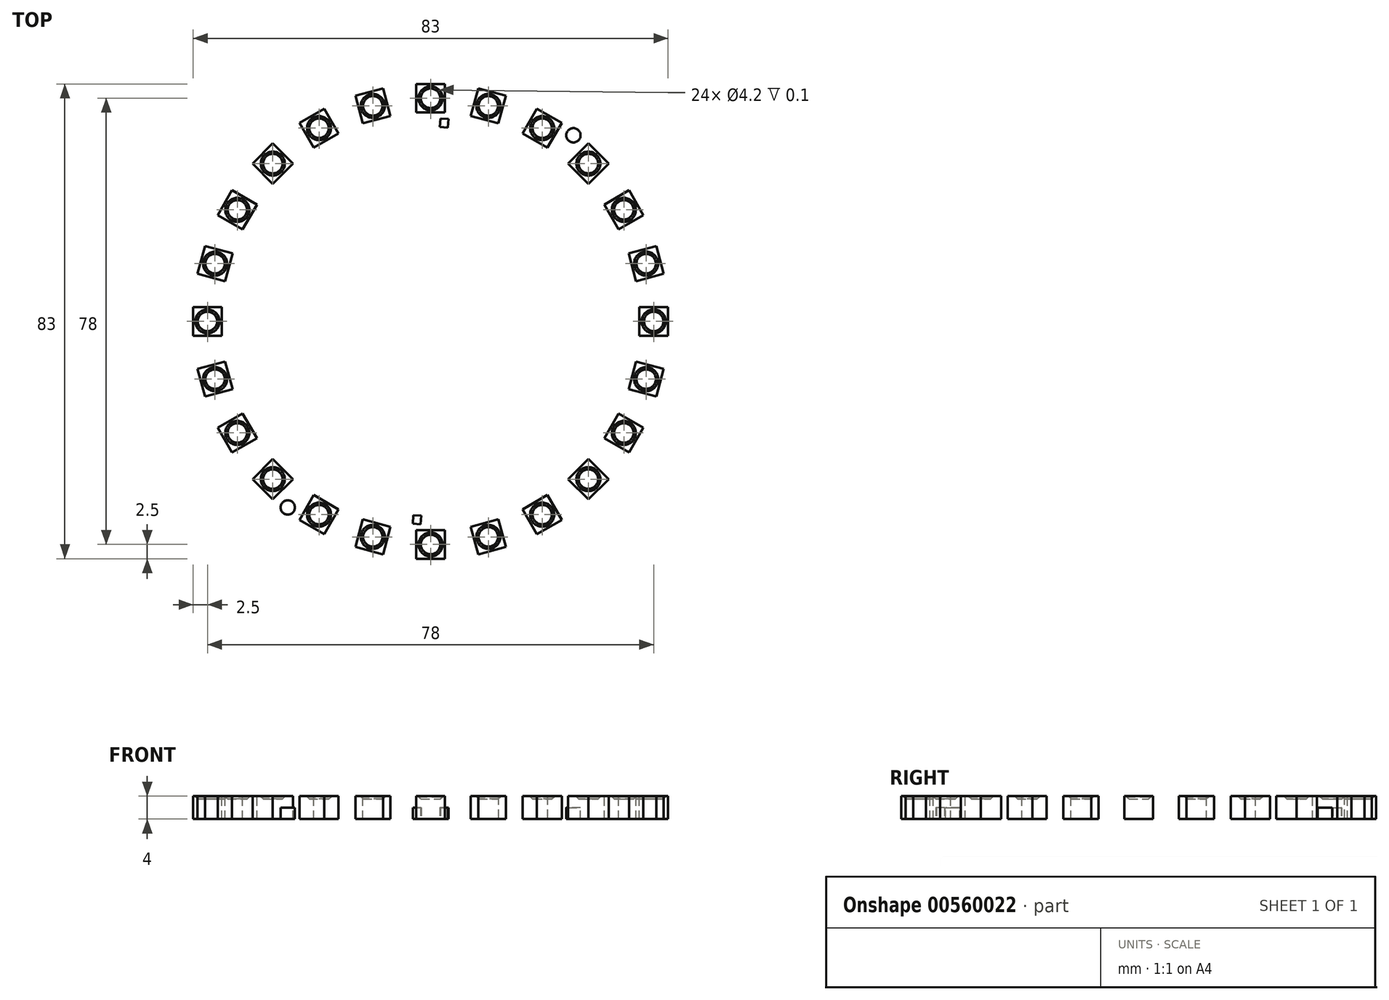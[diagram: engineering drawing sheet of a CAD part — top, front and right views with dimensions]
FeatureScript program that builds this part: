
annotation { "Feature Type Name" : "Feature", "Feature Type Description" : "" }
export const myFeature = defineFeature(function(context is Context, id is Id, definition is map)
    precondition{}
    {
        {
            var Q0;
            Q0=qCreatedBy(makeId("Top.planeOp"),FACE);
            var sketch = newSketch(context, id + "F0", { "sketchPlane" : qUnion([Q0])});
            skCircle(sketch, "E0", {"center": v(0, 0) * mm, "radius": 35.5 * mm});
            skCircle(sketch, "E1", {"center": v(0, 0) * mm, "radius": 42.5 * mm});
            skSolve(sketch);
        }
        {
            var Q0;
            Q0=makeQuery(id+"F0.imprint","IMPRINT",FACE,{"disambiguationData":[TD([[makeQuery(id+"F0.imprint","IMPRINT",EDGE,{"derivedFrom":sQuery(id+"F0.wireOp",EDGE,"E0")}),-1.0]])]});
            extrude(context, id + "F1", {"entities" : qUnion([Q0]), "depth" : 2 * mm, "offsetDistance" : 25 * mm});
        }
        {
            var Q0;
            Q0=makeQuery(id+"F1.opExtrude","CAP_FACE",FACE,{"disambiguationData":[OSD([sQuery(id+"F0.wireOp",EDGE,"E0"),sQuery(id+"F0.wireOp",EDGE,"E1")])],"isStart":false});
            var sketch = newSketch(context, id + "F2", { "sketchPlane" : qUnion([Q0])});
            skLineSegment(sketch, "E2.bottom", {"start": v(2.5, 36.5) * mm, "end": v(-2.5, 36.5) * mm});
            skLineSegment(sketch, "E2.top", {"start": v(2.5, 41.5) * mm, "end": v(-2.5, 41.5) * mm});
            skLineSegment(sketch, "E2.left", {"start": v(2.5, 36.5) * mm, "end": v(2.5, 41.5) * mm});
            skLineSegment(sketch, "E2.right", {"start": v(-2.5, 36.5) * mm, "end": v(-2.5, 41.5) * mm});
            skPoint(sketch, "E2.middle", {"position": v(0, 39) * mm});
            skSolve(sketch);
        }
        {
            var Q0;
            Q0 = qSketchRegion(id + "F2", true);
            extrude(context, id + "F3", {"entities" : qUnion([Q0]), "depth" : 2 * mm, "offsetDistance" : 25 * mm});
        }
        {
            var Q0;
            Q0=makeQuery(id+"F3.opExtrude","CAP_FACE",FACE,{"disambiguationData":[OSD([sQuery(id+"F2.wireOp",EDGE,"E2.bottom"),sQuery(id+"F2.wireOp",EDGE,"E2.top"),sQuery(id+"F2.wireOp",EDGE,"E2.left"),sQuery(id+"F2.wireOp",EDGE,"E2.right")])],"isStart":false});
            var sketch = newSketch(context, id + "F4", { "sketchPlane" : qUnion([Q0])});
            skCircle(sketch, "E3", {"center": v(0, 39) * mm, "radius": 2.1 * mm});
            skPoint(sketch, "E3.centerSnap0", {"position": v(2.5, 39) * mm});
            skPoint(sketch, "E3.centerSnap1", {"position": v(0, 41.5) * mm});
            skSolve(sketch);
        }
        {
            var Q0;
            Q0=makeQuery(id+"F4.imprint","IMPRINT",FACE,{"disambiguationData":[TD([[makeQuery(id+"F4.imprint","IMPRINT",EDGE,{"derivedFrom":sQuery(id+"F4.wireOp",EDGE,"E3")}),1.0]])]});
            extrude(context, id + "F5", {"entities" : qUnion([Q0]), "operationType" : NewBodyOperationType.REMOVE, "oppositeDirection" : true, "depth" : 0.5 * mm, "offsetDistance" : 25 * mm});
        }
        {
            var Q0;
            Q0=makeQuery(id+"F5.boolean.opBoolean","COPY",EDGE,{"derivedFrom":makeQuery(id+"F5.opExtrude","CAP_EDGE",EDGE,{"disambiguationData":[OSD([sQuery(id+"F4.wireOp",EDGE,"E3")])],"isStart":false})});
            chamfer(context, id + "F6", {"entities" : qUnion([Q0]), "width" : 0.4 * mm, "tangentPropagation" : true});
        }
        {
            var Q0;
            Q0=makeQuery(id+"F3.opExtrude","SWEPT_BODY",BODY,{"disambiguationData":[OSD([sQuery(id+"F2.wireOp",EDGE,"E2.bottom"),sQuery(id+"F2.wireOp",EDGE,"E2.top"),sQuery(id+"F2.wireOp",EDGE,"E2.left"),sQuery(id+"F2.wireOp",EDGE,"E2.right")])]});
            var Q1;
            Q1=makeQuery(id+"F1.opExtrude","CAP_EDGE",EDGE,{"disambiguationData":[OSD([sQuery(id+"F0.wireOp",EDGE,"E0")])],"isStart":false});
            circularPattern(context, id + "F7", {"operationType" : NewBodyOperationType.ADD, "entities" : qUnion([Q0]), "axis" : qUnion([Q1]), "angle" : 360 * degree, "instanceCount" : 24, "equalSpace" : true});
        }
        {
            var Q0;
            Q0=makeQuery(id+"F1.opExtrude","CAP_FACE",FACE,{"disambiguationData":[OSD([sQuery(id+"F0.wireOp",EDGE,"E0"),sQuery(id+"F0.wireOp",EDGE,"E1")])],"isStart":false});
            var sketch = newSketch(context, id + "F8", { "sketchPlane" : qUnion([Q0])});
            skLineSegment(sketch, "E4", {"start": v(0, 61.56) * mm, "end": v(0, -60.15) * mm, "construction": true});
            skLineSegment(sketch, "E5", {"start": v(64.53, 0) * mm, "end": v(-72.37, 0) * mm, "construction": true});
            skCircle(sketch, "E6.0", {"center": v(0, 0) * mm, "radius": 42.5 * mm, "construction": true});
            skCircle(sketch, "E7.0", {"center": v(0, 0) * mm, "radius": 35.5 * mm, "construction": true});
            skCircle(sketch, "E8.0", {"center": v(0, 0) * mm, "radius": 41 * mm, "construction": true});
            skCircle(sketch, "E9", {"center": v(-24.96, 32.53) * mm, "radius": 1.25 * mm});
            skPoint(sketch, "E10.0", {"position": v(-22.92, 34.7) * mm});
            skPoint(sketch, "E11.0", {"position": v(-27.58, 31.11) * mm});
            skCircle(sketch, "E12.MirrorC", {"center": v(24.96, 32.53) * mm, "radius": 1.25 * mm});
            skCircle(sketch, "E13.MirrorC", {"center": v(-24.96, -32.53) * mm, "radius": 1.25 * mm});
            skCircle(sketch, "E14.MirrorC", {"center": v(24.96, -32.53) * mm, "radius": 1.25 * mm});
            skSolve(sketch);
        }
        {
            var Q0;
            Q0=makeQuery(id+"F8.imprint","IMPRINT",FACE,{"disambiguationData":[TD([[makeQuery(id+"F8.imprint","IMPRINT",EDGE,{"derivedFrom":sQuery(id+"F8.wireOp",EDGE,"E9")}),1.0]])]});
            var Q1;
            Q1=makeQuery(id+"F8.imprint","IMPRINT",FACE,{"disambiguationData":[TD([[makeQuery(id+"F8.imprint","IMPRINT",EDGE,{"derivedFrom":sQuery(id+"F8.wireOp",EDGE,"E12.MirrorC")}),-1.0]])]});
            var Q2;
            Q2=makeQuery(id+"F8.imprint","IMPRINT",FACE,{"disambiguationData":[TD([[makeQuery(id+"F8.imprint","IMPRINT",EDGE,{"derivedFrom":sQuery(id+"F8.wireOp",EDGE,"E13.MirrorC")}),-1.0]])]});
            var Q3;
            Q3=makeQuery(id+"F8.imprint","IMPRINT",FACE,{"disambiguationData":[TD([[makeQuery(id+"F8.imprint","IMPRINT",EDGE,{"derivedFrom":sQuery(id+"F8.wireOp",EDGE,"E14.MirrorC")}),1.0]])]});
            extrude(context, id + "F9", {"entities" : qUnion([Q0, Q1, Q2, Q3]), "operationType" : NewBodyOperationType.REMOVE, "oppositeDirection" : true, "depth" : 25 * mm, "offsetDistance" : 25 * mm});
        }
        {
            var Q0;
            Q0=makeQuery(id+"F1.opExtrude","CAP_FACE",FACE,{"disambiguationData":[OSD([sQuery(id+"F0.wireOp",EDGE,"E0"),sQuery(id+"F0.wireOp",EDGE,"E1")])],"isStart":true});
            var sketch = newSketch(context, id + "F10", { "sketchPlane" : qUnion([Q0])});
            skLineSegment(sketch, "E15.0.0", {"start": v(2.5, -36.5) * mm, "end": v(2.5, -41.5) * mm, "construction": true});
            skLineSegment(sketch, "E15.0.1", {"start": v(2.5, -41.5) * mm, "end": v(-2.5, -41.5) * mm, "construction": true});
            skLineSegment(sketch, "E15.0.2", {"start": v(-2.5, -41.5) * mm, "end": v(-2.5, -36.5) * mm, "construction": true});
            skLineSegment(sketch, "E15.0.3", {"start": v(-2.5, -36.5) * mm, "end": v(2.5, -36.5) * mm, "construction": true});
            skCircle(sketch, "E16.0", {"center": v(0, 0) * mm, "radius": 35.5 * mm, "construction": true});
            skLineSegment(sketch, "E17.0.0", {"start": v(-2.5, 36.5) * mm, "end": v(-2.5, 41.5) * mm, "construction": true});
            skLineSegment(sketch, "E17.0.1", {"start": v(-2.5, 41.5) * mm, "end": v(2.5, 41.5) * mm, "construction": true});
            skLineSegment(sketch, "E17.0.2", {"start": v(2.5, 41.5) * mm, "end": v(2.5, 36.5) * mm, "construction": true});
            skLineSegment(sketch, "E17.0.3", {"start": v(2.5, 36.5) * mm, "end": v(-2.5, 36.5) * mm, "construction": true});
            skLineSegment(sketch, "E18", {"start": v(2.5, -36.5) * mm, "end": v(-2.5, 36.5) * mm, "construction": true});
            skCircle(sketch, "E19.0.0", {"center": v(0, 0) * mm, "radius": 42.5 * mm});
            skLineSegment(sketch, "E20", {"start": v(3.02, -33.87) * mm, "end": v(3.12, -35.36) * mm});
            skLineSegment(sketch, "E21", {"start": v(1.63, -33.96) * mm, "end": v(1.73, -35.46) * mm});
            skLineSegment(sketch, "E22", {"start": v(3.02, -33.87) * mm, "end": v(2.32, -33.91) * mm});
            skLineSegment(sketch, "E23", {"start": v(2.32, -33.91) * mm, "end": v(1.63, -33.96) * mm});
            skLineSegment(sketch, "E24", {"start": v(0, 0) * mm, "end": v(17.5, 1.2) * mm, "construction": true});
            skLineSegment(sketch, "E25", {"start": v(1.73, -35.46) * mm, "end": v(3.12, -35.36) * mm});
            skLineSegment(sketch, "E26.MirrorCS", {"start": v(-3.02, 33.87) * mm, "end": v(-3.12, 35.36) * mm});
            skLineSegment(sketch, "E27.MirrorCS", {"start": v(-3.12, 35.36) * mm, "end": v(-1.73, 35.46) * mm});
            skLineSegment(sketch, "E28.MirrorCS", {"start": v(-1.63, 33.96) * mm, "end": v(-1.73, 35.46) * mm});
            skLineSegment(sketch, "E29.MirrorCS", {"start": v(-1.63, 33.96) * mm, "end": v(-2.32, 33.91) * mm});
            skLineSegment(sketch, "E30.MirrorCS", {"start": v(-2.32, 33.91) * mm, "end": v(-3.02, 33.87) * mm});
            skSolve(sketch);
        }
        {
            var Q0;
            Q0=makeQuery(id+"F10.imprint","IMPRINT",FACE,{"disambiguationData":[TD([[makeQuery(id+"F10.imprint","IMPRINT",EDGE,{"derivedFrom":sQuery(id+"F10.wireOp",EDGE,"E26.MirrorCS")}),-1.0]])]});
            var Q1;
            Q1=makeQuery(id+"F10.imprint","IMPRINT",FACE,{"disambiguationData":[TD([[makeQuery(id+"F10.imprint","IMPRINT",EDGE,{"derivedFrom":sQuery(id+"F10.wireOp",EDGE,"E20")}),-1.0]])]});
            var Q2;
            Q2=makeQuery(id+"F1.opExtrude","CAP_FACE",FACE,{"disambiguationData":[OSD([sQuery(id+"F0.wireOp",EDGE,"E0"),sQuery(id+"F0.wireOp",EDGE,"E1")])],"isStart":false});
            extrude(context, id + "F11", {"entities" : qUnion([Q0, Q1]), "operationType" : NewBodyOperationType.ADD, "endBound" : BoundingType.UP_TO_SURFACE, "oppositeDirection" : true, "depth" : 25 * mm, "endBoundEntityFace" : qUnion([Q2]), "offsetDistance" : 25 * mm});
        }
    });
